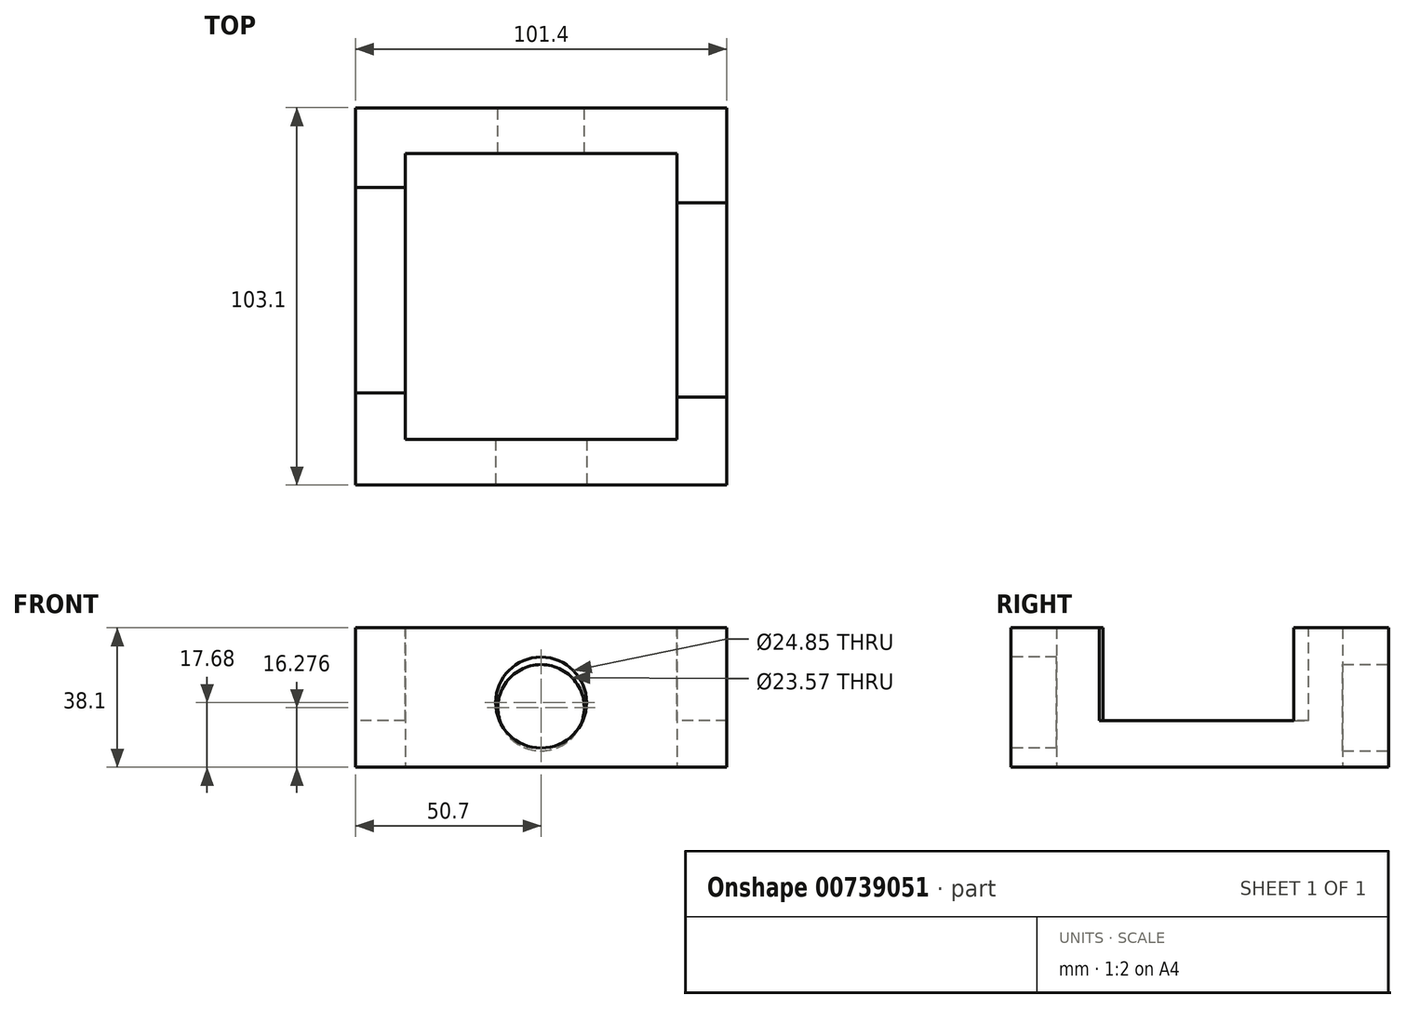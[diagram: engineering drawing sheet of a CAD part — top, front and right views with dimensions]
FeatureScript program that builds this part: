
annotation { "Feature Type Name" : "Feature", "Feature Type Description" : "" }
export const myFeature = defineFeature(function(context is Context, id is Id, definition is map)
    precondition{}
    {
        {
            var Q0;
            Q0=qCreatedBy(makeId("Top.planeOp"),FACE);
            var sketch = newSketch(context, id + "F0", { "sketchPlane" : qUnion([Q0])});
            skLineSegment(sketch, "E0.bottom", {"start": v(50.7, 51.55) * mm, "end": v(-50.7, 51.55) * mm});
            skLineSegment(sketch, "E0.top", {"start": v(50.7, -51.55) * mm, "end": v(-50.7, -51.55) * mm});
            skLineSegment(sketch, "E0.left", {"start": v(50.7, 51.55) * mm, "end": v(50.7, -51.55) * mm});
            skLineSegment(sketch, "E0.right", {"start": v(-50.7, 51.55) * mm, "end": v(-50.7, -51.55) * mm});
            skPoint(sketch, "E0.middle", {"position": v(0, 0) * mm});
            skLineSegment(sketch, "E1.bottom", {"start": v(37.1, -39.08) * mm, "end": v(-37.1, -39.08) * mm});
            skLineSegment(sketch, "E1.top", {"start": v(37.1, 39.08) * mm, "end": v(-37.1, 39.08) * mm});
            skLineSegment(sketch, "E1.left", {"start": v(37.1, -39.08) * mm, "end": v(37.1, 39.08) * mm});
            skLineSegment(sketch, "E1.right", {"start": v(-37.1, -39.08) * mm, "end": v(-37.1, 39.08) * mm});
            skSolve(sketch);
        }
        {
            var Q0;
            Q0 = qSketchRegion(id + "F0", true);
            extrude(context, id + "F1", {"entities" : qUnion([Q0]), "depth" : 38.1 * mm, "offsetDistance" : 25.4 * mm});
        }
        {
            var Q0;
            Q0=makeQuery(id+"F1.opExtrude","CAP_FACE",FACE,{"disambiguationData":[OSD([sQuery(id+"F0.wireOp",EDGE,"E0.bottom"),sQuery(id+"F0.wireOp",EDGE,"E0.top"),sQuery(id+"F0.wireOp",EDGE,"E0.left"),sQuery(id+"F0.wireOp",EDGE,"E0.right"),sQuery(id+"F0.wireOp",EDGE,"E1.bottom"),sQuery(id+"F0.wireOp",EDGE,"E1.top"),sQuery(id+"F0.wireOp",EDGE,"E1.left"),sQuery(id+"F0.wireOp",EDGE,"E1.right")])],"isStart":false});
            var sketch = newSketch(context, id + "F2", { "sketchPlane" : qUnion([Q0])});
            skLineSegment(sketch, "E2", {"start": v(50.7, -27.45) * mm, "end": v(37.1, -27.45) * mm});
            skLineSegment(sketch, "E3", {"start": v(92.54, 9.97) * mm, "end": v(92.54, -22.87) * mm});
            skLineSegment(sketch, "E4", {"start": v(92.54, -22.87) * mm, "end": v(92.54, 9.97) * mm});
            skLineSegment(sketch, "E5", {"start": v(50.7, 25.62) * mm, "end": v(37.1, 25.62) * mm});
            skLineSegment(sketch, "E6", {"start": v(-37.1, 29.7) * mm, "end": v(-50.7, 29.7) * mm});
            skLineSegment(sketch, "E7", {"start": v(-37.1, -26.36) * mm, "end": v(-50.7, -26.36) * mm});
            skSolve(sketch);
        }
        {
            var Q0;
            {var subQ0=sQuery(id+"F2.wireOp",EDGE,"E6");Q0=makeQuery(id+"F2.imprint","IMPRINT",FACE,{"disambiguationData":[TD([[makeQuery(id+"F2.imprint","IMPRINT",EDGE,{"derivedFrom":subQ0}),1.0]])]});}
            extrude(context, id + "F3", {"entities" : qUnion([Q0]), "operationType" : NewBodyOperationType.REMOVE, "oppositeDirection" : true, "depth" : 25.4 * mm, "offsetDistance" : 25.4 * mm});
        }
        {
            var Q0;
            {var subQ0=sQuery(id+"F2.wireOp",EDGE,"E2");Q0=makeQuery(id+"F2.imprint","IMPRINT",FACE,{"disambiguationData":[TD([[makeQuery(id+"F2.imprint","IMPRINT",EDGE,{"derivedFrom":subQ0}),-1.0]])]});}
            var Q1;
            Q1 = qSketchRegion(id + "F2", true);
            extrude(context, id + "F4", {"entities" : qUnion([Q0, Q1]), "operationType" : NewBodyOperationType.REMOVE, "oppositeDirection" : true, "depth" : 25.4 * mm, "offsetDistance" : 25.4 * mm});
        }
        {
            var Q0;
            Q0=makeQuery(id+"F1.opExtrude","SWEPT_FACE",FACE,{"disambiguationData":[OSD([sQuery(id+"F0.wireOp",EDGE,"E0.top")])]});
            var sketch = newSketch(context, id + "F5", { "sketchPlane" : qUnion([Q0])});
            skCircle(sketch, "E8", {"center": v(0, 17.68) * mm, "radius": 12.42 * mm});
            skSolve(sketch);
        }
        {
            var Q0;
            Q0 = qSketchRegion(id + "F5", true);
            extrude(context, id + "F6", {"entities" : qUnion([Q0]), "operationType" : NewBodyOperationType.REMOVE, "oppositeDirection" : true, "depth" : 25.4 * mm, "offsetDistance" : 25.4 * mm});
        }
        {
            var Q0;
            Q0=makeQuery(id+"F1.opExtrude","SWEPT_FACE",FACE,{"disambiguationData":[OSD([sQuery(id+"F0.wireOp",EDGE,"E0.bottom")])]});
            var sketch = newSketch(context, id + "F7", { "sketchPlane" : qUnion([Q0])});
            skCircle(sketch, "E9", {"center": v(0, 16.28) * mm, "radius": 11.78 * mm});
            skPoint(sketch, "E9.centerSnap0", {"position": v(0, 38.1) * mm});
            skSolve(sketch);
        }
        {
            var Q0;
            Q0=makeQuery(id+"F7.imprint","IMPRINT",FACE,{"disambiguationData":[TD([[makeQuery(id+"F7.imprint","IMPRINT",EDGE,{"derivedFrom":sQuery(id+"F7.wireOp",EDGE,"E9")}),1.0]])]});
            extrude(context, id + "F8", {"entities" : qUnion([Q0]), "operationType" : NewBodyOperationType.REMOVE, "oppositeDirection" : true, "depth" : 25.4 * mm, "offsetDistance" : 25.4 * mm});
        }
    });
